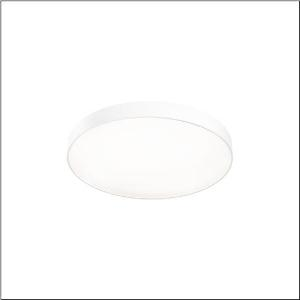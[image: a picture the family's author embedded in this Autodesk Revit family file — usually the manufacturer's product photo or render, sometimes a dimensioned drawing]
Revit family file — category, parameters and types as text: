
# Revit family: round_21_m_51mr36gd0421w
name_source: partatom
category: Lighting Fixtures
units: mm (PartAtom-declared; Revit-internal decimal feet)

## family parameters
Cut with Voids When Loaded = No
Host = Face
Light Source = No
Part Type = Normal
Room Calculation Point = No
Round Connector Dimension = Use Diameter
Shared = No

## types (1)
- Round 21 M (1 x LED, 7870 lm, 54.6 W, 4000K)
    Apparent Load = 55 VA
    CIE Flux Codes = 49 80 96 85 100
    Color Rendering = 80
    Color Temperature = 4000K
    Default Elevation = 1800 mm
    Description = Round 21 M, wall and ceiling luminaire, primary optical cover: cover, of PMMA, opal, light emission: direct/indirect distribution, primary light characteristic: symmetric, installation type: suspended mounting, surface-mounted, LED, rated luminous flux: 7.870lm, luminous efficacy: 144lm/W, light colour: 840, colour temperature: 4000K, control gear: DALI 2, with terminal, 5-pole, mains connection: 230V, AC, 50/60Hz, rated input power: 54.6W, housing, of aluminium, coated, white, diameter: 600mm, height: 62mm, protection rating (complete): IP40, insulation class (complete): insulation class I (protective earthing), certification: CE, impact resistance: IK04, permissible operating ambient temperature: -10..+35°C, packaging unit: 1 piece
    Height = 87 mm
    Lamp = 1 x LED
    Lamp Light Flux = 7870 lm
    Lamp Power = 54.6 W
    Lamp count = 1
    Length = 600 mm
    Luminous efficacy = 144 lm/W
    Manufacturer = Siteco
    ModVariant = No
    Model = 51MR36GD0421W
    Mounting Place = Ceiling
    Mounting Type = Surface mounted
    Number of Poles = 1
    OnlyDefault = Yes
    Power Factor = 1
    Product Name = Round 21 M
    Product group = wall and ceiling luminaire | ceiling mounted
    ProductGroupID = 304
    Protection Class = Protection class I
    Protection Degree = IP 40
    RLX_Detail_Level = 1
    RLX_Emergency_Light_Flux = 0 lm
    RLX_Emergency_Type = 0
    RLX_Emergency_Type_DB = No
    RlxData = <blob elided: 12145 chars, md5=a19bce88>
    Socket = socket
    Standby Power = 0 W
    System Light Flux = 7870 lm
    System Power = 55 W
    Type Comments = Product without accessories
    Type Image = l_1258330.jpg
    URL = http://relux.com
    VarID = ---
    Voltage = 0 V
    Weight = 0.00 kg
    Width = 0 mm  [stored 0 ft]

note: [stored X ft] marks values corroborated as IEEE doubles in the binary element streams (Revit-internal decimal feet)

## geometry (parser evidence)
native form markers: Sweep x12
no freeform markers — native parametric forms only
